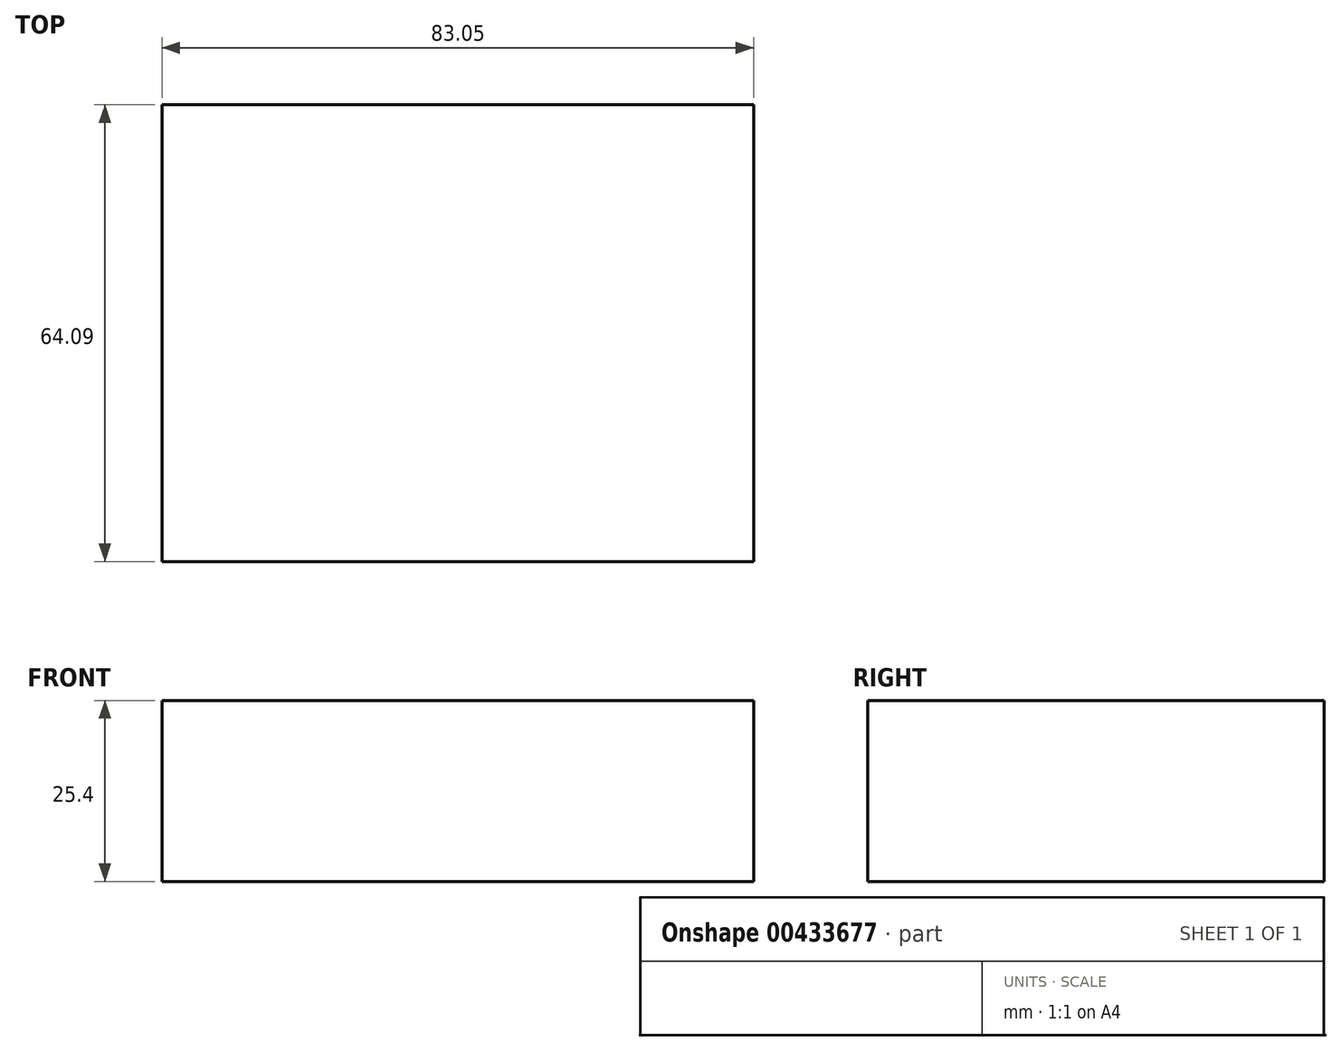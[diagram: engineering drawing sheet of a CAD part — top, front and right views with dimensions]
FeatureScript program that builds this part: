
annotation { "Feature Type Name" : "Feature", "Feature Type Description" : "" }
export const myFeature = defineFeature(function(context is Context, id is Id, definition is map)
    precondition{}
    {
        {
            var Q0;
            Q0=qCreatedBy(makeId("Top.planeOp"),FACE);
            var sketch = newSketch(context, id + "F0", { "sketchPlane" : qUnion([Q0])});
            skLineSegment(sketch, "E0.bottom", {"start": v(0, 0) * mm, "end": v(-83.05, 0) * mm});
            skLineSegment(sketch, "E0.top", {"start": v(0, 64.1) * mm, "end": v(-83.05, 64.1) * mm});
            skLineSegment(sketch, "E0.left", {"start": v(0, 0) * mm, "end": v(0, 64.1) * mm});
            skLineSegment(sketch, "E0.right", {"start": v(-83.05, 0) * mm, "end": v(-83.05, 64.1) * mm});
            skSolve(sketch);
        }
        {
            var Q0;
            Q0=makeQuery(id+"F0.imprint","IMPRINT",FACE,{"disambiguationData":[TD([[makeQuery(id+"F0.imprint","IMPRINT",EDGE,{"derivedFrom":sQuery(id+"F0.wireOp",EDGE,"E0.bottom")}),-1.0]])]});
            extrude(context, id + "F1", {"entities" : qUnion([Q0]), "depth" : 25.4 * mm});
        }
    });
